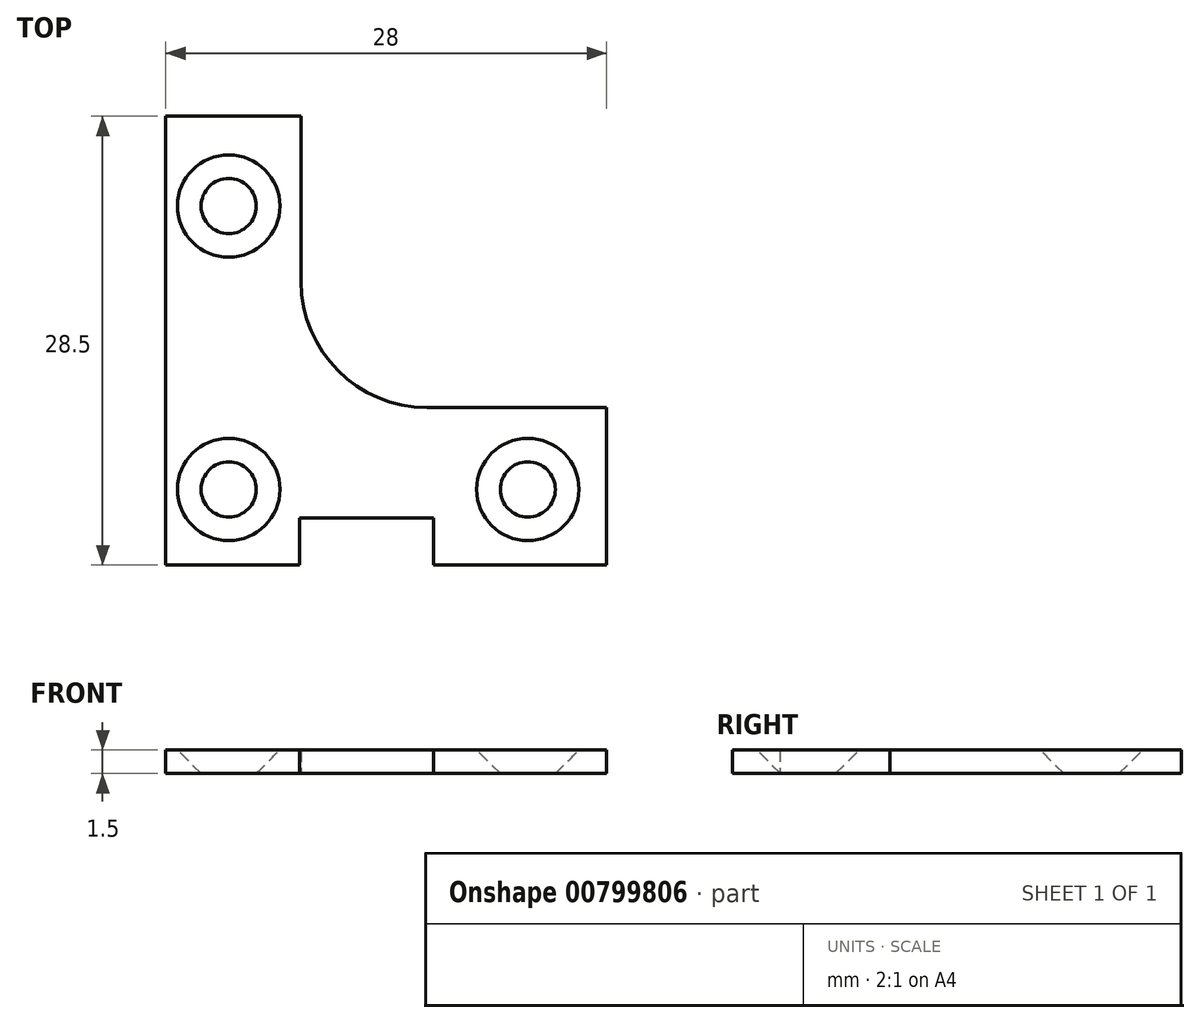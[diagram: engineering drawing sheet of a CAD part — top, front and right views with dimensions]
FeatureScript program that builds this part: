
annotation { "Feature Type Name" : "Feature", "Feature Type Description" : "" }
export const myFeature = defineFeature(function(context is Context, id is Id, definition is map)
    precondition{}
    {
        {
            var Q0;
            Q0=qCreatedBy(makeId("Top.planeOp"),FACE);
            var sketch = newSketch(context, id + "F0", { "sketchPlane" : qUnion([Q0])});
            skLineSegment(sketch, "E0", {"start": v(0, 0) * mm, "end": v(0, 28.5) * mm});
            skLineSegment(sketch, "E1", {"start": v(0, 28.5) * mm, "end": v(8.6, 28.5) * mm});
            skLineSegment(sketch, "E2", {"start": v(0, 0) * mm, "end": v(8.5, 0) * mm});
            skLineSegment(sketch, "E3", {"start": v(8.5, 0) * mm, "end": v(8.5, 3) * mm});
            skLineSegment(sketch, "E4", {"start": v(8.5, 3) * mm, "end": v(17, 3) * mm});
            skLineSegment(sketch, "E5", {"start": v(17, 3) * mm, "end": v(17, 0) * mm});
            skLineSegment(sketch, "E6", {"start": v(17, 0) * mm, "end": v(28, 0) * mm});
            skLineSegment(sketch, "E7", {"start": v(28, 0) * mm, "end": v(28, 10) * mm});
            skLineSegment(sketch, "E8", {"start": v(28, 10) * mm, "end": v(8.6, 10) * mm});
            skLineSegment(sketch, "E9", {"start": v(8.6, 10) * mm, "end": v(8.6, 28.5) * mm});
            skCircle(sketch, "E10", {"center": v(4, 4.8) * mm, "radius": 1.75 * mm});
            skCircle(sketch, "E11", {"center": v(23, 4.8) * mm, "radius": 1.75 * mm});
            skCircle(sketch, "E12", {"center": v(4, 22.8) * mm, "radius": 1.75 * mm});
            skSolve(sketch);
        }
        {
            var Q0;
            Q0=makeQuery(id+"F0.imprint","IMPRINT",FACE,{"disambiguationData":[TD([[makeQuery(id+"F0.imprint","IMPRINT",EDGE,{"derivedFrom":sQuery(id+"F0.wireOp",EDGE,"E0")}),-1.0]])]});
            extrude(context, id + "F1", {"entities" : qUnion([Q0]), "depth" : 1.5 * mm, "offsetDistance" : 25 * mm});
        }
        {
            var Q0;
            Q0=makeQuery(id+"F1.opExtrude","CAP_EDGE",EDGE,{"disambiguationData":[OSD([sQuery(id+"F0.wireOp",EDGE,"E12")])],"isStart":false});
            var Q1;
            Q1=makeQuery(id+"F1.opExtrude","CAP_EDGE",EDGE,{"disambiguationData":[OSD([sQuery(id+"F0.wireOp",EDGE,"E10")])],"isStart":false});
            var Q2;
            Q2=makeQuery(id+"F1.opExtrude","CAP_EDGE",EDGE,{"disambiguationData":[OSD([sQuery(id+"F0.wireOp",EDGE,"E11")])],"isStart":false});
            chamfer(context, id + "F2", {"entities" : qUnion([Q0, Q1, Q2]), "width" : 1.5 * mm, "tangentPropagation" : true});
        }
        {
            var Q0;
            Q0=makeQuery(id+"F1.opExtrude","SWEPT_EDGE",EDGE,{"disambiguationData":[OSD([sQuery(id+"F0.wireOp",EDGE,"E8"),sQuery(id+"F0.wireOp",EDGE,"E9")])]});
            fillet(context, id + "F3", {"entities" : qUnion([Q0]), "radius" : 8 * mm, "tangentPropagation" : true, "allowEdgeOverflow" : false});
        }
    });
